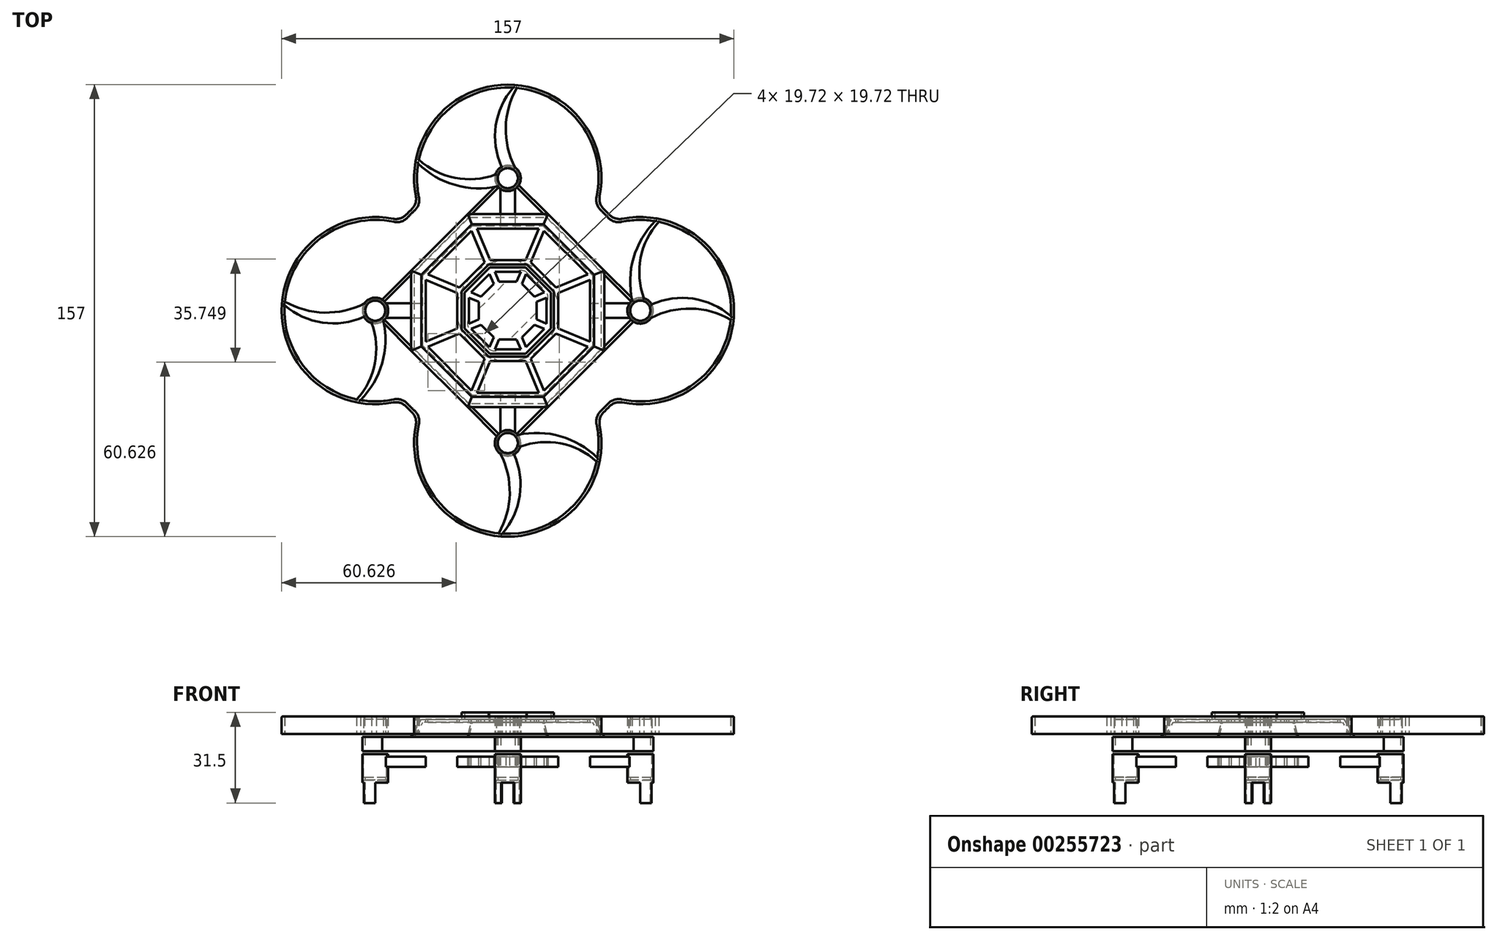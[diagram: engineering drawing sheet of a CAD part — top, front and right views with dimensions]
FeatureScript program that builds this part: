
annotation { "Feature Type Name" : "Feature", "Feature Type Description" : "" }
export const myFeature = defineFeature(function(context is Context, id is Id, definition is map)
    precondition{}
    {
        {
            var Q0;
            Q0=qCreatedBy(makeId("Top.planeOp"),FACE);
            var sketch = newSketch(context, id + "F0", { "sketchPlane" : qUnion([Q0])});
            skArc(sketch, "E0", {"start": v(4.7, -16.86) * mm, "mid": v(12.37, -12.37) * mm, "end": v(16.86, -4.7) * mm});
            skLineSegment(sketch, "E1.left", {"start": v(-2.5, 42.26) * mm, "end": v(-2.5, 19.75) * mm});
            skLineSegment(sketch, "E1.right", {"start": v(2.5, 42.26) * mm, "end": v(2.5, 19.75) * mm});
            skArc(sketch, "E2", {"start": v(42.26, -2.5) * mm, "mid": v(50.5, 0) * mm, "end": v(42.26, 2.5) * mm});
            skArc(sketch, "E3", {"start": v(-42.26, 2.5) * mm, "mid": v(-50.5, 0) * mm, "end": v(-42.26, -2.5) * mm});
            skArc(sketch, "E4", {"start": v(2.5, 42.26) * mm, "mid": v(0, 50.5) * mm, "end": v(-2.5, 42.26) * mm});
            skArc(sketch, "E5", {"start": v(-2.5, -42.26) * mm, "mid": v(0, -50.5) * mm, "end": v(2.5, -42.26) * mm});
            skArc(sketch, "E6.trimOffspring", {"start": v(-16.86, -4.7) * mm, "mid": v(-12.37, -12.37) * mm, "end": v(-4.7, -16.86) * mm});
            skArc(sketch, "E7.trimOffspring", {"start": v(16.86, 4.7) * mm, "mid": v(12.37, 12.37) * mm, "end": v(4.7, 16.86) * mm});
            skArc(sketch, "E8.trimOffspring", {"start": v(-4.7, 16.86) * mm, "mid": v(-12.37, 12.37) * mm, "end": v(-16.86, 4.7) * mm});
            skLineSegment(sketch, "E9", {"start": v(-42.26, 2.5) * mm, "end": v(-19.75, 2.5) * mm});
            skLineSegment(sketch, "E10", {"start": v(-42.26, -2.5) * mm, "end": v(-19.75, -2.5) * mm});
            skLineSegment(sketch, "E11", {"start": v(-42.26, 2.5) * mm, "end": v(-42.26, -2.5) * mm, "construction": true});
            skPoint(sketch, "E12", {"position": v(-42.26, 0) * mm});
            skLineSegment(sketch, "E13", {"start": v(-46, 0) * mm, "end": v(46, 0) * mm, "construction": true});
            skLineSegment(sketch, "E14", {"start": v(0, 46) * mm, "end": v(0, -46) * mm, "construction": true});
            skLineSegment(sketch, "E15", {"start": v(19.75, 2.5) * mm, "end": v(42.26, 2.5) * mm});
            skLineSegment(sketch, "E16", {"start": v(19.75, -2.5) * mm, "end": v(42.26, -2.5) * mm});
            skLineSegment(sketch, "E17", {"start": v(42.26, 2.5) * mm, "end": v(42.26, -2.5) * mm, "construction": true});
            skPoint(sketch, "E18", {"position": v(42.26, 0) * mm});
            skPoint(sketch, "E19.visualSharp", {"position": v(-17.32, 2.5) * mm});
            skArc(sketch, "E19.filletArc", {"start": v(-19.75, 2.5) * mm, "mid": v(-17.93, 3.11) * mm, "end": v(-16.86, 4.7) * mm});
            skPoint(sketch, "E20.visualSharp", {"position": v(17.32, 2.5) * mm});
            skArc(sketch, "E20.filletArc", {"start": v(16.86, 4.7) * mm, "mid": v(17.93, 3.11) * mm, "end": v(19.75, 2.5) * mm});
            skPoint(sketch, "E21.visualSharp", {"position": v(17.32, -2.5) * mm});
            skArc(sketch, "E21.filletArc", {"start": v(19.75, -2.5) * mm, "mid": v(17.93, -3.11) * mm, "end": v(16.86, -4.7) * mm});
            skPoint(sketch, "E22.visualSharp", {"position": v(-17.32, -2.5) * mm});
            skArc(sketch, "E22.filletArc", {"start": v(-16.86, -4.7) * mm, "mid": v(-17.93, -3.11) * mm, "end": v(-19.75, -2.5) * mm});
            skPoint(sketch, "E23.visualSharp", {"position": v(-2.5, 17.32) * mm});
            skArc(sketch, "E23.filletArc", {"start": v(-4.7, 16.86) * mm, "mid": v(-3.11, 17.93) * mm, "end": v(-2.5, 19.75) * mm});
            skPoint(sketch, "E24.visualSharp", {"position": v(2.5, 17.32) * mm});
            skArc(sketch, "E24.filletArc", {"start": v(2.5, 19.75) * mm, "mid": v(3.11, 17.93) * mm, "end": v(4.7, 16.86) * mm});
            skPoint(sketch, "E25.visualSharp", {"position": v(-2.5, -17.32) * mm});
            skArc(sketch, "E25.filletArc", {"start": v(-2.5, -19.75) * mm, "mid": v(-3.11, -17.93) * mm, "end": v(-4.7, -16.86) * mm});
            skPoint(sketch, "E26.visualSharp", {"position": v(2.5, -17.32) * mm});
            skArc(sketch, "E26.filletArc", {"start": v(4.7, -16.86) * mm, "mid": v(3.11, -17.93) * mm, "end": v(2.5, -19.75) * mm});
            skLineSegment(sketch, "E27", {"start": v(-2.5, -19.75) * mm, "end": v(-2.5, -42.26) * mm});
            skLineSegment(sketch, "E28", {"start": v(2.5, -19.75) * mm, "end": v(2.5, -42.26) * mm});
            skLineSegment(sketch, "E29", {"start": v(-2.5, -42.26) * mm, "end": v(2.5, -42.26) * mm, "construction": true});
            skPoint(sketch, "E30", {"position": v(0, -42.26) * mm});
            skLineSegment(sketch, "E31", {"start": v(-2.5, 42.26) * mm, "end": v(2.5, 42.26) * mm, "construction": true});
            skPoint(sketch, "E32", {"position": v(0, 42.26) * mm});
            skLineSegment(sketch, "E33", {"start": v(-13.08, -2.47) * mm, "end": v(2.47, 13.08) * mm});
            skLineSegment(sketch, "E34", {"start": v(6.72, 13.08) * mm, "end": v(13.08, 6.72) * mm});
            skLineSegment(sketch, "E35", {"start": v(13.08, 2.47) * mm, "end": v(-2.47, -13.08) * mm});
            skLineSegment(sketch, "E36", {"start": v(-6.72, -13.08) * mm, "end": v(-13.08, -6.72) * mm});
            skLineSegment(sketch, "E37", {"start": v(15.2, 4.6) * mm, "end": v(-15.2, -4.6) * mm, "construction": true});
            skLineSegment(sketch, "E38", {"start": v(4.6, 15.2) * mm, "end": v(-4.6, -15.2) * mm, "construction": true});
            skLineSegment(sketch, "E39", {"start": v(9.9, 9.9) * mm, "end": v(-9.9, -9.9) * mm, "construction": true});
            skPoint(sketch, "E40.visualSharp", {"position": v(4.6, 15.2) * mm});
            skArc(sketch, "E40.filletArc", {"start": v(6.72, 13.08) * mm, "mid": v(4.6, 13.96) * mm, "end": v(2.47, 13.08) * mm});
            skPoint(sketch, "E41.visualSharp", {"position": v(-15.2, -4.6) * mm});
            skArc(sketch, "E41.filletArc", {"start": v(-13.08, -2.47) * mm, "mid": v(-13.96, -4.6) * mm, "end": v(-13.08, -6.72) * mm});
            skPoint(sketch, "E42.visualSharp", {"position": v(-4.6, -15.2) * mm});
            skArc(sketch, "E42.filletArc", {"start": v(-6.72, -13.08) * mm, "mid": v(-4.6, -13.96) * mm, "end": v(-2.47, -13.08) * mm});
            skPoint(sketch, "E43.visualSharp", {"position": v(15.2, 4.6) * mm});
            skArc(sketch, "E43.filletArc", {"start": v(13.08, 2.47) * mm, "mid": v(13.96, 4.6) * mm, "end": v(13.08, 6.72) * mm});
            skSolve(sketch);
        }
        {
            var Q0;
            Q0=makeQuery(id+"F0.imprint","IMPRINT",FACE,{"disambiguationData":[TD([[makeQuery(id+"F0.imprint","IMPRINT",EDGE,{"derivedFrom":sQuery(id+"F0.wireOp",EDGE,"E0")}),1.0]])]});
            extrude(context, id + "F1", {"entities" : qUnion([Q0]), "depth" : 3.5 * mm});
        }
        {
            var Q0;
            Q0=makeQuery(id+"F1.opExtrude","CAP_FACE",FACE,{"disambiguationData":[OSD([sQuery(id+"F0.wireOp",EDGE,"E0"),sQuery(id+"F0.wireOp",EDGE,"E1.left"),sQuery(id+"F0.wireOp",EDGE,"E1.right"),sQuery(id+"F0.wireOp",EDGE,"E2"),sQuery(id+"F0.wireOp",EDGE,"E3"),sQuery(id+"F0.wireOp",EDGE,"E4"),sQuery(id+"F0.wireOp",EDGE,"E5"),sQuery(id+"F0.wireOp",EDGE,"E6.trimOffspring"),sQuery(id+"F0.wireOp",EDGE,"E7.trimOffspring"),sQuery(id+"F0.wireOp",EDGE,"E8.trimOffspring"),sQuery(id+"F0.wireOp",EDGE,"E9"),sQuery(id+"F0.wireOp",EDGE,"E10"),sQuery(id+"F0.wireOp",EDGE,"E15"),sQuery(id+"F0.wireOp",EDGE,"E16"),sQuery(id+"F0.wireOp",EDGE,"E19.filletArc"),sQuery(id+"F0.wireOp",EDGE,"E20.filletArc"),sQuery(id+"F0.wireOp",EDGE,"E21.filletArc"),sQuery(id+"F0.wireOp",EDGE,"E22.filletArc"),sQuery(id+"F0.wireOp",EDGE,"E23.filletArc"),sQuery(id+"F0.wireOp",EDGE,"E24.filletArc"),sQuery(id+"F0.wireOp",EDGE,"E25.filletArc"),sQuery(id+"F0.wireOp",EDGE,"E26.filletArc"),sQuery(id+"F0.wireOp",EDGE,"E27"),sQuery(id+"F0.wireOp",EDGE,"E28"),sQuery(id+"F0.wireOp",EDGE,"E33"),sQuery(id+"F0.wireOp",EDGE,"E34"),sQuery(id+"F0.wireOp",EDGE,"E35"),sQuery(id+"F0.wireOp",EDGE,"E36"),sQuery(id+"F0.wireOp",EDGE,"E40.filletArc"),sQuery(id+"F0.wireOp",EDGE,"E41.filletArc"),sQuery(id+"F0.wireOp",EDGE,"E42.filletArc"),sQuery(id+"F0.wireOp",EDGE,"E43.filletArc")])],"isStart":true});
            var sketch = newSketch(context, id + "F2", { "sketchPlane" : qUnion([Q0])});
            skCircle(sketch, "E44", {"center": v(-46, 0) * mm, "radius": 4.5 * mm});
            skCircle(sketch, "E45", {"center": v(0, 46) * mm, "radius": 4.5 * mm});
            skCircle(sketch, "E46", {"center": v(46, 0) * mm, "radius": 4.5 * mm});
            skCircle(sketch, "E47", {"center": v(0, -46) * mm, "radius": 4.5 * mm});
            skSolve(sketch);
        }
        {
            var Q0;
            Q0=qSketchRegion(id+"F2",true);
            extrude(context, id + "F3", {"entities" : qUnion([Q0]), "operationType" : NewBodyOperationType.ADD, "oppositeDirection" : true, "depth" : 4.45 * mm, "hasSecondDirection" : true, "secondDirectionOppositeDirection" : false, "secondDirectionDepth" : (10 - 4.45) * mm});
        }
        {
            var Q0;
            Q0=makeQuery(id+"F3.opExtrude","CAP_FACE",FACE,{"disambiguationData":[OSD([sQuery(id+"F2.wireOp",EDGE,"E45")])],"isStart":true});
            var sketch = newSketch(context, id + "F4", { "sketchPlane" : qUnion([Q0])});
            skArc(sketch, "E48", {"start": v(4.5, 46) * mm, "mid": v(3.9, 48.25) * mm, "end": v(2.25, 49.9) * mm});
            skArc(sketch, "E49", {"start": v(4, 46) * mm, "mid": v(3.46, 48) * mm, "end": v(2, 49.46) * mm});
            skLineSegment(sketch, "E50", {"start": v(2, 49.46) * mm, "end": v(2.25, 49.9) * mm});
            skLineSegment(sketch, "E51", {"start": v(-2, 49.46) * mm, "end": v(-2.25, 49.9) * mm});
            skLineSegment(sketch, "E52", {"start": v(-4, 46) * mm, "end": v(-4.5, 46) * mm});
            skLineSegment(sketch, "E53", {"start": v(4, 46) * mm, "end": v(4.5, 46) * mm});
            skLineSegment(sketch, "E54", {"start": v(0, 46) * mm, "end": v(0, 50.5) * mm, "construction": true});
            skArc(sketch, "E55.trimOffspring", {"start": v(-2, 49.46) * mm, "mid": v(-3.46, 48) * mm, "end": v(-4, 46) * mm});
            skArc(sketch, "E56.trimOffspring", {"start": v(-2.25, 49.9) * mm, "mid": v(-3.9, 48.25) * mm, "end": v(-4.5, 46) * mm});
            skLineSegment(sketch, "E57.1.0", {"start": v(-46, 0) * mm, "end": v(-50.5, 0) * mm, "construction": true});
            skArc(sketch, "E57.1.1", {"start": v(-46, 4.5) * mm, "mid": v(-48.25, 3.9) * mm, "end": v(-49.9, 2.25) * mm});
            skArc(sketch, "E57.1.2", {"start": v(-46, 4) * mm, "mid": v(-48, 3.46) * mm, "end": v(-49.46, 2) * mm});
            skArc(sketch, "E57.1.3", {"start": v(-49.9, -2.25) * mm, "mid": v(-48.25, -3.9) * mm, "end": v(-46, -4.5) * mm});
            skArc(sketch, "E57.1.4", {"start": v(-49.46, -2) * mm, "mid": v(-48, -3.46) * mm, "end": v(-46, -4) * mm});
            skLineSegment(sketch, "E57.1.5", {"start": v(-46, -4) * mm, "end": v(-46, -4.5) * mm});
            skLineSegment(sketch, "E57.1.6", {"start": v(-46, 4) * mm, "end": v(-46, 4.5) * mm});
            skLineSegment(sketch, "E57.1.7", {"start": v(-49.46, 2) * mm, "end": v(-49.9, 2.25) * mm});
            skLineSegment(sketch, "E57.1.8", {"start": v(-49.46, -2) * mm, "end": v(-49.9, -2.25) * mm});
            skLineSegment(sketch, "E57.2.0", {"start": v(0, -46) * mm, "end": v(0, -50.5) * mm, "construction": true});
            skArc(sketch, "E57.2.1", {"start": v(-4.5, -46) * mm, "mid": v(-3.9, -48.25) * mm, "end": v(-2.25, -49.9) * mm});
            skArc(sketch, "E57.2.2", {"start": v(-4, -46) * mm, "mid": v(-3.46, -48) * mm, "end": v(-2, -49.46) * mm});
            skArc(sketch, "E57.2.3", {"start": v(2.25, -49.9) * mm, "mid": v(3.9, -48.25) * mm, "end": v(4.5, -46) * mm});
            skArc(sketch, "E57.2.4", {"start": v(2, -49.46) * mm, "mid": v(3.46, -48) * mm, "end": v(4, -46) * mm});
            skLineSegment(sketch, "E57.2.5", {"start": v(4, -46) * mm, "end": v(4.5, -46) * mm});
            skLineSegment(sketch, "E57.2.6", {"start": v(-4, -46) * mm, "end": v(-4.5, -46) * mm});
            skLineSegment(sketch, "E57.2.7", {"start": v(-2, -49.46) * mm, "end": v(-2.25, -49.9) * mm});
            skLineSegment(sketch, "E57.2.8", {"start": v(2, -49.46) * mm, "end": v(2.25, -49.9) * mm});
            skLineSegment(sketch, "E57.3.0", {"start": v(46, 0) * mm, "end": v(50.5, 0) * mm, "construction": true});
            skArc(sketch, "E57.3.1", {"start": v(46, -4.5) * mm, "mid": v(48.25, -3.9) * mm, "end": v(49.9, -2.25) * mm});
            skArc(sketch, "E57.3.2", {"start": v(46, -4) * mm, "mid": v(48, -3.46) * mm, "end": v(49.46, -2) * mm});
            skArc(sketch, "E57.3.3", {"start": v(49.9, 2.25) * mm, "mid": v(48.25, 3.9) * mm, "end": v(46, 4.5) * mm});
            skArc(sketch, "E57.3.4", {"start": v(49.46, 2) * mm, "mid": v(48, 3.46) * mm, "end": v(46, 4) * mm});
            skLineSegment(sketch, "E57.3.5", {"start": v(46, 4) * mm, "end": v(46, 4.5) * mm});
            skLineSegment(sketch, "E57.3.6", {"start": v(46, -4) * mm, "end": v(46, -4.5) * mm});
            skLineSegment(sketch, "E57.3.7", {"start": v(49.46, -2) * mm, "end": v(49.9, -2.25) * mm});
            skLineSegment(sketch, "E57.3.8", {"start": v(49.46, 2) * mm, "end": v(49.9, 2.25) * mm});
            skPoint(sketch, "E57.center", {"position": v(0, 0) * mm});
            skSolve(sketch);
        }
        {
            var Q0;
            Q0=qSketchRegion(id+"F4",true);
            extrude(context, id + "F5", {"entities" : qUnion([Q0]), "operationType" : NewBodyOperationType.ADD, "depth" : 7 * mm});
        }
        {
            var Q0;
            Q0=makeQuery(id+"F3.opExtrude","CAP_FACE",FACE,{"disambiguationData":[OSD([sQuery(id+"F2.wireOp",EDGE,"E46")])],"isStart":true});
            var sketch = newSketch(context, id + "F6", { "sketchPlane" : qUnion([Q0])});
            skCircle(sketch, "E58", {"center": v(46, 0) * mm, "radius": 4 * mm});
            skCircle(sketch, "E59.1.0", {"center": v(0, 46) * mm, "radius": 4 * mm});
            skCircle(sketch, "E59.2.0", {"center": v(-46, 0) * mm, "radius": 4 * mm});
            skCircle(sketch, "E59.3.0", {"center": v(0, -46) * mm, "radius": 4 * mm});
            skPoint(sketch, "E59.center", {"position": v(0, 0) * mm});
            skSolve(sketch);
        }
        {
            var Q0;
            Q0=qSketchRegion(id+"F6",true);
            extrude(context, id + "F7", {"entities" : qUnion([Q0]), "operationType" : NewBodyOperationType.REMOVE, "endBound" : BoundingType.UP_TO_NEXT, "oppositeDirection" : true, "depth" : 25 * mm});
        }
        {
            var Q0;
            {var subQ0=sQuery(id+"F2.wireOp",EDGE,"E46");Q0=makeQuery(id+"F7.boolean.opBoolean","SPLIT",FACE,{"disambiguationData":[TD([makeQuery(id+"F5.opExtrude","SWEPT_FACE",FACE,{"disambiguationData":[OSD([sQuery(id+"F4.wireOp",EDGE,"E57.3.5")])]})])],"derivedFrom":makeQuery(id+"F3.opExtrude","CAP_FACE",FACE,{"disambiguationData":[OSD([subQ0])],"isStart":true})});}
            cPlane(context, id + "F8", {"entities" : qUnion([Q0]), "cplaneType" : CPlaneType.OFFSET, "offset" : 1 * mm, "oppositeDirection" : true, "width" : 150 * mm, "height" : 150 * mm});
        }
        {
            var Q0;
            Q0=qCreatedBy(id+"F8.planeOp",FACE);
            var sketch = newSketch(context, id + "F9", { "sketchPlane" : qUnion([Q0])});
            skCircle(sketch, "E60", {"center": v(46, 0) * mm, "radius": 4 * mm});
            skCircle(sketch, "E61", {"center": v(46, 0) * mm, "radius": 3.5 * mm});
            skCircle(sketch, "E62.1.0", {"center": v(0, 46) * mm, "radius": 3.5 * mm});
            skCircle(sketch, "E62.1.1", {"center": v(0, 46) * mm, "radius": 4 * mm});
            skCircle(sketch, "E62.2.0", {"center": v(-46, 0) * mm, "radius": 3.5 * mm});
            skCircle(sketch, "E62.2.1", {"center": v(-46, 0) * mm, "radius": 4 * mm});
            skCircle(sketch, "E62.3.0", {"center": v(0, -46) * mm, "radius": 3.5 * mm});
            skCircle(sketch, "E62.3.1", {"center": v(0, -46) * mm, "radius": 4 * mm});
            skPoint(sketch, "E62.center", {"position": v(0, 0) * mm});
            skSolve(sketch);
        }
        {
            var Q0;
            Q0=qSketchRegion(id+"F9",true);
            extrude(context, id + "F10", {"entities" : qUnion([Q0]), "operationType" : NewBodyOperationType.ADD, "oppositeDirection" : true, "depth" : 1 * mm});
        }
        {
            var Q0;
            Q0=makeQuery(id+"F3.opExtrude","CAP_FACE",FACE,{"disambiguationData":[OSD([sQuery(id+"F2.wireOp",EDGE,"E45")])],"isStart":false});
            cPlane(context, id + "F11", {"entities" : qUnion([Q0]), "cplaneType" : CPlaneType.OFFSET, "offset" : 7 * mm, "width" : 150 * mm, "height" : 150 * mm});
        }
        {
            var Q0;
            Q0=qCreatedBy(id+"F11.planeOp",FACE);
            var sketch = newSketch(context, id + "F12", { "sketchPlane" : qUnion([Q0])});
            skArc(sketch, "E63", {"start": v(3.5, -43.18) * mm, "mid": v(-3.32, -42.96) * mm, "end": v(-2.51, -49.73) * mm});
            skCircle(sketch, "E64", {"center": v(0, -46) * mm, "radius": 4 * mm});
            skArc(sketch, "E65", {"start": v(-30.1, -36.74) * mm, "mid": v(-26.23, -63.44) * mm, "end": v(-3.12, -77.35) * mm});
            skArc(sketch, "E66", {"start": v(30.1, -36.74) * mm, "mid": v(33.59, -33.59) * mm, "end": v(36.74, -30.1) * mm});
            skArc(sketch, "E67", {"start": v(49.95, 2.16) * mm, "mid": v(41.5, 0.2) * mm, "end": v(49.73, -2.51) * mm});
            skCircle(sketch, "E68", {"center": v(46, 0) * mm, "radius": 4 * mm});
            skCircle(sketch, "E69", {"center": v(0, 46) * mm, "radius": 4.5 * mm});
            skCircle(sketch, "E70", {"center": v(0, 46) * mm, "radius": 4 * mm});
            skCircle(sketch, "E71", {"center": v(-46, 0) * mm, "radius": 4.5 * mm});
            skCircle(sketch, "E72", {"center": v(-46, 0) * mm, "radius": 4 * mm});
            skArc(sketch, "E73", {"start": v(36.74, -30.1) * mm, "mid": v(63.44, -26.23) * mm, "end": v(77.35, -3.12) * mm});
            skArc(sketch, "E74", {"start": v(30.1, 36.74) * mm, "mid": v(0, 77.5) * mm, "end": v(-30.1, 36.74) * mm});
            skArc(sketch, "E75", {"start": v(-36.74, 30.1) * mm, "mid": v(-77.5, 0) * mm, "end": v(-36.74, -30.1) * mm});
            skArc(sketch, "E76.trimOffspring", {"start": v(36.74, 30.1) * mm, "mid": v(33.59, 33.59) * mm, "end": v(30.1, 36.74) * mm});
            skArc(sketch, "E77.trimOffspring", {"start": v(-30.1, 36.74) * mm, "mid": v(-33.59, 33.59) * mm, "end": v(-36.74, 30.1) * mm});
            skArc(sketch, "E78.trimOffspring", {"start": v(-36.74, -30.1) * mm, "mid": v(-33.59, -33.59) * mm, "end": v(-30.1, -36.74) * mm});
            skArc(sketch, "E79.0", {"start": v(-37.09, -31.25) * mm, "mid": v(-34.3, -34.3) * mm, "end": v(-31.25, -37.09) * mm});
            skArc(sketch, "E79.1", {"start": v(-37.09, 31.25) * mm, "mid": v(-78.5, 0) * mm, "end": v(-37.09, -31.25) * mm});
            skArc(sketch, "E79.2", {"start": v(-31.25, -37.09) * mm, "mid": v(0, -78.5) * mm, "end": v(31.25, -37.09) * mm});
            skArc(sketch, "E79.3", {"start": v(-31.25, 37.09) * mm, "mid": v(-34.3, 34.3) * mm, "end": v(-37.09, 31.25) * mm});
            skArc(sketch, "E79.4", {"start": v(31.25, -37.09) * mm, "mid": v(34.3, -34.3) * mm, "end": v(37.09, -31.25) * mm});
            skArc(sketch, "E79.5", {"start": v(37.09, -31.25) * mm, "mid": v(78.5, 0) * mm, "end": v(37.09, 31.25) * mm});
            skArc(sketch, "E79.6", {"start": v(37.09, 31.25) * mm, "mid": v(34.3, 34.3) * mm, "end": v(31.25, 37.09) * mm});
            skArc(sketch, "E79.7", {"start": v(31.25, 37.09) * mm, "mid": v(0, 78.5) * mm, "end": v(-31.25, 37.09) * mm});
            skArc(sketch, "E80", {"start": v(30.84, -52.42) * mm, "mid": v(18.3, -46.12) * mm, "end": v(4.32, -47.25) * mm});
            skArc(sketch, "E81", {"start": v(31.08, -51.12) * mm, "mid": v(18.3, -43.64) * mm, "end": v(3.5, -43.18) * mm});
            skArc(sketch, "E82", {"start": v(-1.88, -77.44) * mm, "mid": v(4.15, -64.29) * mm, "end": v(2.16, -49.95) * mm});
            skArc(sketch, "E83", {"start": v(-3.12, -77.35) * mm, "mid": v(0.69, -63.62) * mm, "end": v(-2.51, -49.73) * mm});
            skArc(sketch, "E84.1.0", {"start": v(52.42, 30.84) * mm, "mid": v(46.12, 18.3) * mm, "end": v(47.25, 4.32) * mm});
            skArc(sketch, "E84.1.1", {"start": v(51.12, 31.08) * mm, "mid": v(43.64, 18.3) * mm, "end": v(43.18, 3.5) * mm});
            skArc(sketch, "E84.1.2", {"start": v(77.44, -1.88) * mm, "mid": v(64.29, 4.15) * mm, "end": v(49.95, 2.16) * mm});
            skArc(sketch, "E84.1.3", {"start": v(77.35, -3.12) * mm, "mid": v(63.62, 0.69) * mm, "end": v(49.73, -2.51) * mm});
            skArc(sketch, "E84.2.0", {"start": v(-30.84, 52.42) * mm, "mid": v(-18.3, 46.12) * mm, "end": v(-4.32, 47.25) * mm});
            skArc(sketch, "E84.2.1", {"start": v(-31.08, 51.12) * mm, "mid": v(-18.3, 43.64) * mm, "end": v(-3.5, 43.18) * mm});
            skArc(sketch, "E84.2.2", {"start": v(1.88, 77.44) * mm, "mid": v(-4.15, 64.29) * mm, "end": v(-2.16, 49.95) * mm});
            skArc(sketch, "E84.2.3", {"start": v(3.12, 77.35) * mm, "mid": v(-0.69, 63.62) * mm, "end": v(2.51, 49.73) * mm});
            skArc(sketch, "E84.3.0", {"start": v(-52.42, -30.84) * mm, "mid": v(-46.12, -18.3) * mm, "end": v(-47.25, -4.32) * mm});
            skArc(sketch, "E84.3.1", {"start": v(-51.12, -31.08) * mm, "mid": v(-43.64, -18.3) * mm, "end": v(-43.18, -3.5) * mm});
            skArc(sketch, "E84.3.2", {"start": v(-77.44, 1.88) * mm, "mid": v(-64.29, -4.15) * mm, "end": v(-49.95, -2.16) * mm});
            skArc(sketch, "E84.3.3", {"start": v(-77.35, 3.12) * mm, "mid": v(-63.62, -0.69) * mm, "end": v(-49.73, 2.51) * mm});
            skArc(sketch, "E85.trimOffspring", {"start": v(31.08, -51.12) * mm, "mid": v(31.43, -43.88) * mm, "end": v(30.1, -36.74) * mm});
            skArc(sketch, "E86.trimOffspring", {"start": v(-1.88, -77.44) * mm, "mid": v(19.13, -71.02) * mm, "end": v(30.84, -52.42) * mm});
            skArc(sketch, "E87.trimOffspring", {"start": v(2.16, -49.95) * mm, "mid": v(3.51, -48.82) * mm, "end": v(4.32, -47.25) * mm});
            skArc(sketch, "E88.trimOffspring", {"start": v(77.44, -1.88) * mm, "mid": v(71.02, 19.13) * mm, "end": v(52.42, 30.84) * mm});
            skArc(sketch, "E89.trimOffspring", {"start": v(51.12, 31.08) * mm, "mid": v(43.88, 31.43) * mm, "end": v(36.74, 30.1) * mm});
            skSolve(sketch);
        }
        {
            var Q0;
            {var subQ0=sQuery(id+"F12.wireOp",EDGE,"E84.2.2");Q0=makeQuery(id+"F12.imprint","IMPRINT",FACE,{"disambiguationData":[TD([[makeQuery(id+"F12.imprint","IMPRINT",EDGE,{"derivedFrom":subQ0}),1.0]])]});}
            var Q1;
            Q1=makeQuery(id+"F12.imprint","IMPRINT",FACE,{"disambiguationData":[TD([[makeQuery(id+"F12.imprint","IMPRINT",EDGE,{"derivedFrom":sQuery(id+"F12.wireOp",EDGE,"E70")}),-1.0]])]});
            var Q2;
            {var subQ0=sQuery(id+"F12.wireOp",EDGE,"E84.2.0");Q2=makeQuery(id+"F12.imprint","IMPRINT",FACE,{"disambiguationData":[TD([[makeQuery(id+"F12.imprint","IMPRINT",EDGE,{"derivedFrom":subQ0}),-1.0]])]});}
            var Q3;
            Q3=makeQuery(id+"F12.imprint","IMPRINT",FACE,{"disambiguationData":[TD([[makeQuery(id+"F12.imprint","IMPRINT",EDGE,{"derivedFrom":sQuery(id+"F12.wireOp",EDGE,"E63")}),1.0]])]});
            var Q4;
            {var subQ0=sQuery(id+"F12.wireOp",EDGE,"E84.3.0");Q4=makeQuery(id+"F12.imprint","IMPRINT",FACE,{"disambiguationData":[TD([[makeQuery(id+"F12.imprint","IMPRINT",EDGE,{"derivedFrom":subQ0}),-1.0]])]});}
            var Q5;
            {var subQ0=sQuery(id+"F12.wireOp",EDGE,"E84.3.2");Q5=makeQuery(id+"F12.imprint","IMPRINT",FACE,{"disambiguationData":[TD([[makeQuery(id+"F12.imprint","IMPRINT",EDGE,{"derivedFrom":subQ0}),1.0]])]});}
            var Q6;
            Q6=makeQuery(id+"F12.imprint","IMPRINT",FACE,{"disambiguationData":[TD([[makeQuery(id+"F12.imprint","IMPRINT",EDGE,{"derivedFrom":sQuery(id+"F12.wireOp",EDGE,"E72")}),-1.0]])]});
            extrude(context, id + "F13", {"entities" : qUnion([Q0, Q1, Q2, Q3, Q4, Q5, Q6]), "depth" : 6 * mm});
        }
        {
            var Q0;
            Q0=makeQuery(id+"F13.opExtrude","SWEPT_EDGE",EDGE,{"disambiguationData":[OSD([sQuery(id+"F12.wireOp",EDGE,"E66"),sQuery(id+"F12.wireOp",EDGE,"E73")])]});
            var Q1;
            Q1=makeQuery(id+"F13.opExtrude","SWEPT_EDGE",EDGE,{"disambiguationData":[OSD([sQuery(id+"F12.wireOp",EDGE,"E66"),sQuery(id+"F12.wireOp",EDGE,"E85.trimOffspring")])]});
            var Q2;
            Q2=makeQuery(id+"F13.opExtrude","SWEPT_EDGE",EDGE,{"disambiguationData":[OSD([sQuery(id+"F12.wireOp",EDGE,"E79.4"),sQuery(id+"F12.wireOp",EDGE,"E79.5")])]});
            var Q3;
            Q3=makeQuery(id+"F13.opExtrude","SWEPT_EDGE",EDGE,{"disambiguationData":[OSD([sQuery(id+"F12.wireOp",EDGE,"E79.2"),sQuery(id+"F12.wireOp",EDGE,"E79.4")])]});
            var Q4;
            Q4=makeQuery(id+"F13.opExtrude","SWEPT_EDGE",EDGE,{"disambiguationData":[OSD([sQuery(id+"F12.wireOp",EDGE,"E75"),sQuery(id+"F12.wireOp",EDGE,"E78.trimOffspring")])]});
            var Q5;
            Q5=makeQuery(id+"F13.opExtrude","SWEPT_EDGE",EDGE,{"disambiguationData":[OSD([sQuery(id+"F12.wireOp",EDGE,"E65"),sQuery(id+"F12.wireOp",EDGE,"E78.trimOffspring")])]});
            var Q6;
            Q6=makeQuery(id+"F13.opExtrude","SWEPT_EDGE",EDGE,{"disambiguationData":[OSD([sQuery(id+"F12.wireOp",EDGE,"E79.0"),sQuery(id+"F12.wireOp",EDGE,"E79.2")])]});
            var Q7;
            Q7=makeQuery(id+"F13.opExtrude","SWEPT_EDGE",EDGE,{"disambiguationData":[OSD([sQuery(id+"F12.wireOp",EDGE,"E79.0"),sQuery(id+"F12.wireOp",EDGE,"E79.1")])]});
            var Q8;
            Q8=makeQuery(id+"F13.opExtrude","SWEPT_EDGE",EDGE,{"disambiguationData":[OSD([sQuery(id+"F12.wireOp",EDGE,"E79.1"),sQuery(id+"F12.wireOp",EDGE,"E79.3")])]});
            var Q9;
            Q9=makeQuery(id+"F13.opExtrude","SWEPT_EDGE",EDGE,{"disambiguationData":[OSD([sQuery(id+"F12.wireOp",EDGE,"E79.3"),sQuery(id+"F12.wireOp",EDGE,"E79.7")])]});
            var Q10;
            Q10=makeQuery(id+"F13.opExtrude","SWEPT_EDGE",EDGE,{"disambiguationData":[OSD([sQuery(id+"F12.wireOp",EDGE,"E75"),sQuery(id+"F12.wireOp",EDGE,"E77.trimOffspring")])]});
            var Q11;
            Q11=makeQuery(id+"F13.opExtrude","SWEPT_EDGE",EDGE,{"disambiguationData":[OSD([sQuery(id+"F12.wireOp",EDGE,"E74"),sQuery(id+"F12.wireOp",EDGE,"E77.trimOffspring")])]});
            var Q12;
            Q12=makeQuery(id+"F13.opExtrude","SWEPT_EDGE",EDGE,{"disambiguationData":[OSD([sQuery(id+"F12.wireOp",EDGE,"E74"),sQuery(id+"F12.wireOp",EDGE,"E76.trimOffspring")])]});
            var Q13;
            Q13=makeQuery(id+"F13.opExtrude","SWEPT_EDGE",EDGE,{"disambiguationData":[OSD([sQuery(id+"F12.wireOp",EDGE,"E76.trimOffspring"),sQuery(id+"F12.wireOp",EDGE,"E89.trimOffspring")])]});
            var Q14;
            Q14=makeQuery(id+"F13.opExtrude","SWEPT_EDGE",EDGE,{"disambiguationData":[OSD([sQuery(id+"F12.wireOp",EDGE,"E79.6"),sQuery(id+"F12.wireOp",EDGE,"E79.7")])]});
            var Q15;
            Q15=makeQuery(id+"F13.opExtrude","SWEPT_EDGE",EDGE,{"disambiguationData":[OSD([sQuery(id+"F12.wireOp",EDGE,"E79.5"),sQuery(id+"F12.wireOp",EDGE,"E79.6")])]});
            fillet(context, id + "F14", {"entities" : qUnion([Q0, Q1, Q2, Q3, Q4, Q5, Q6, Q7, Q8, Q9, Q10, Q11, Q12, Q13, Q14, Q15]), "radius" : 5 * mm, "tangentPropagation" : true, "allowEdgeOverflow" : false});
        }
        {
            var Q0;
            Q0=makeQuery(id+"F13.opExtrude","CAP_FACE",FACE,{"disambiguationData":[OSD([sQuery(id+"F12.wireOp",EDGE,"E63"),sQuery(id+"F12.wireOp",EDGE,"E64"),sQuery(id+"F12.wireOp",EDGE,"E65"),sQuery(id+"F12.wireOp",EDGE,"E66"),sQuery(id+"F12.wireOp",EDGE,"E67"),sQuery(id+"F12.wireOp",EDGE,"E68"),sQuery(id+"F12.wireOp",EDGE,"E69"),sQuery(id+"F12.wireOp",EDGE,"E70"),sQuery(id+"F12.wireOp",EDGE,"E71"),sQuery(id+"F12.wireOp",EDGE,"E72"),sQuery(id+"F12.wireOp",EDGE,"E73"),sQuery(id+"F12.wireOp",EDGE,"E74"),sQuery(id+"F12.wireOp",EDGE,"E75"),sQuery(id+"F12.wireOp",EDGE,"E76.trimOffspring"),sQuery(id+"F12.wireOp",EDGE,"E77.trimOffspring"),sQuery(id+"F12.wireOp",EDGE,"E78.trimOffspring"),sQuery(id+"F12.wireOp",EDGE,"E79.0"),sQuery(id+"F12.wireOp",EDGE,"E79.1"),sQuery(id+"F12.wireOp",EDGE,"E79.2"),sQuery(id+"F12.wireOp",EDGE,"E79.3"),sQuery(id+"F12.wireOp",EDGE,"E79.4"),sQuery(id+"F12.wireOp",EDGE,"E79.5"),sQuery(id+"F12.wireOp",EDGE,"E79.6"),sQuery(id+"F12.wireOp",EDGE,"E79.7"),sQuery(id+"F12.wireOp",EDGE,"E80"),sQuery(id+"F12.wireOp",EDGE,"E81"),sQuery(id+"F12.wireOp",EDGE,"E82"),sQuery(id+"F12.wireOp",EDGE,"E83"),sQuery(id+"F12.wireOp",EDGE,"E84.1.0"),sQuery(id+"F12.wireOp",EDGE,"E84.1.1"),sQuery(id+"F12.wireOp",EDGE,"E84.1.2"),sQuery(id+"F12.wireOp",EDGE,"E84.1.3"),sQuery(id+"F12.wireOp",EDGE,"E84.2.0"),sQuery(id+"F12.wireOp",EDGE,"E84.2.1"),sQuery(id+"F12.wireOp",EDGE,"E84.2.2"),sQuery(id+"F12.wireOp",EDGE,"E84.2.3"),sQuery(id+"F12.wireOp",EDGE,"E84.3.0"),sQuery(id+"F12.wireOp",EDGE,"E84.3.1"),sQuery(id+"F12.wireOp",EDGE,"E84.3.2"),sQuery(id+"F12.wireOp",EDGE,"E84.3.3"),sQuery(id+"F12.wireOp",EDGE,"E85.trimOffspring"),sQuery(id+"F12.wireOp",EDGE,"E86.trimOffspring"),sQuery(id+"F12.wireOp",EDGE,"E87.trimOffspring"),sQuery(id+"F12.wireOp",EDGE,"E88.trimOffspring"),sQuery(id+"F12.wireOp",EDGE,"E89.trimOffspring")])],"isStart":false});
            var sketch = newSketch(context, id + "F15", { "sketchPlane" : qUnion([Q0])});
            skCircle(sketch, "E90", {"center": v(0, -46) * mm, "radius": 4.5 * mm});
            skCircle(sketch, "E91", {"center": v(0, -46) * mm, "radius": 3.5 * mm});
            skCircle(sketch, "E92.1.0", {"center": v(46, 0) * mm, "radius": 4.5 * mm});
            skCircle(sketch, "E92.1.1", {"center": v(46, 0) * mm, "radius": 3.5 * mm});
            skCircle(sketch, "E92.2.0", {"center": v(0, 46) * mm, "radius": 4.5 * mm});
            skCircle(sketch, "E92.2.1", {"center": v(0, 46) * mm, "radius": 3.5 * mm});
            skCircle(sketch, "E92.3.0", {"center": v(-46, 0) * mm, "radius": 4.5 * mm});
            skCircle(sketch, "E92.3.1", {"center": v(-46, 0) * mm, "radius": 3.5 * mm});
            skPoint(sketch, "E92.center", {"position": v(0, 0) * mm});
            skSolve(sketch);
        }
        {
            var Q0;
            Q0=qSketchRegion(id+"F15",true);
            extrude(context, id + "F16", {"entities" : qUnion([Q0]), "operationType" : NewBodyOperationType.ADD, "oppositeDirection" : true, "depth" : 1 * mm});
        }
        {
            var Q0;
            Q0=makeQuery(id+"F16.boolean.opBoolean","MERGE",FACE,{"derivedFrom":[makeQuery(id+"F13.opExtrude","CAP_FACE",FACE,{"disambiguationData":[OSD([sQuery(id+"F12.wireOp",EDGE,"E63"),sQuery(id+"F12.wireOp",EDGE,"E64"),sQuery(id+"F12.wireOp",EDGE,"E65"),sQuery(id+"F12.wireOp",EDGE,"E66"),sQuery(id+"F12.wireOp",EDGE,"E67"),sQuery(id+"F12.wireOp",EDGE,"E68"),sQuery(id+"F12.wireOp",EDGE,"E69"),sQuery(id+"F12.wireOp",EDGE,"E70"),sQuery(id+"F12.wireOp",EDGE,"E71"),sQuery(id+"F12.wireOp",EDGE,"E72"),sQuery(id+"F12.wireOp",EDGE,"E73"),sQuery(id+"F12.wireOp",EDGE,"E74"),sQuery(id+"F12.wireOp",EDGE,"E75"),sQuery(id+"F12.wireOp",EDGE,"E76.trimOffspring"),sQuery(id+"F12.wireOp",EDGE,"E77.trimOffspring"),sQuery(id+"F12.wireOp",EDGE,"E78.trimOffspring"),sQuery(id+"F12.wireOp",EDGE,"E79.0"),sQuery(id+"F12.wireOp",EDGE,"E79.1"),sQuery(id+"F12.wireOp",EDGE,"E79.2"),sQuery(id+"F12.wireOp",EDGE,"E79.3"),sQuery(id+"F12.wireOp",EDGE,"E79.4"),sQuery(id+"F12.wireOp",EDGE,"E79.5"),sQuery(id+"F12.wireOp",EDGE,"E79.6"),sQuery(id+"F12.wireOp",EDGE,"E79.7"),sQuery(id+"F12.wireOp",EDGE,"E80"),sQuery(id+"F12.wireOp",EDGE,"E81"),sQuery(id+"F12.wireOp",EDGE,"E82"),sQuery(id+"F12.wireOp",EDGE,"E83"),sQuery(id+"F12.wireOp",EDGE,"E84.1.0"),sQuery(id+"F12.wireOp",EDGE,"E84.1.1"),sQuery(id+"F12.wireOp",EDGE,"E84.1.2"),sQuery(id+"F12.wireOp",EDGE,"E84.1.3"),sQuery(id+"F12.wireOp",EDGE,"E84.2.0"),sQuery(id+"F12.wireOp",EDGE,"E84.2.1"),sQuery(id+"F12.wireOp",EDGE,"E84.2.2"),sQuery(id+"F12.wireOp",EDGE,"E84.2.3"),sQuery(id+"F12.wireOp",EDGE,"E84.3.0"),sQuery(id+"F12.wireOp",EDGE,"E84.3.1"),sQuery(id+"F12.wireOp",EDGE,"E84.3.2"),sQuery(id+"F12.wireOp",EDGE,"E84.3.3"),sQuery(id+"F12.wireOp",EDGE,"E85.trimOffspring"),sQuery(id+"F12.wireOp",EDGE,"E86.trimOffspring"),sQuery(id+"F12.wireOp",EDGE,"E87.trimOffspring"),sQuery(id+"F12.wireOp",EDGE,"E88.trimOffspring"),sQuery(id+"F12.wireOp",EDGE,"E89.trimOffspring")])],"isStart":false}),makeQuery(id+"F16.opExtrude","CAP_FACE",FACE,{"disambiguationData":[OSD([sQuery(id+"F15.wireOp",EDGE,"E90"),sQuery(id+"F15.wireOp",EDGE,"E91")])],"isStart":true}),makeQuery(id+"F16.opExtrude","CAP_FACE",FACE,{"disambiguationData":[OSD([sQuery(id+"F15.wireOp",EDGE,"E92.1.0"),sQuery(id+"F15.wireOp",EDGE,"E92.1.1")])],"isStart":true}),makeQuery(id+"F16.opExtrude","CAP_FACE",FACE,{"disambiguationData":[OSD([sQuery(id+"F15.wireOp",EDGE,"E92.2.0"),sQuery(id+"F15.wireOp",EDGE,"E92.2.1")])],"isStart":true}),makeQuery(id+"F16.opExtrude","CAP_FACE",FACE,{"disambiguationData":[OSD([sQuery(id+"F15.wireOp",EDGE,"E92.3.0"),sQuery(id+"F15.wireOp",EDGE,"E92.3.1")])],"isStart":true})]});
            fillet(context, id + "F17", {"entities" : qUnion([Q0]), "radius" : 0.3 * mm, "tangentPropagation" : true, "allowEdgeOverflow" : false});
        }
        {
            var Q0;
            Q0=makeQuery(id+"F3.opExtrude","CAP_FACE",FACE,{"disambiguationData":[OSD([sQuery(id+"F2.wireOp",EDGE,"E45")])],"isStart":false});
            cPlane(context, id + "F18", {"entities" : qUnion([Q0]), "cplaneType" : CPlaneType.OFFSET, "offset" : 1 * mm, "width" : 150 * mm, "height" : 150 * mm});
        }
        {
            var Q0;
            Q0=qCreatedBy(id+"F18.planeOp",FACE);
            var sketch = newSketch(context, id + "F19", { "sketchPlane" : qUnion([Q0])});
            skCircle(sketch, "E93", {"center": v(0, -46) * mm, "radius": 4.5 * mm});
            skCircle(sketch, "E94", {"center": v(0, -46) * mm, "radius": 3.5 * mm});
            skCircle(sketch, "E95.1.0", {"center": v(46, 0) * mm, "radius": 4.5 * mm});
            skCircle(sketch, "E95.1.1", {"center": v(46, 0) * mm, "radius": 3.5 * mm});
            skCircle(sketch, "E95.2.0", {"center": v(0, 46) * mm, "radius": 4.5 * mm});
            skCircle(sketch, "E95.2.1", {"center": v(0, 46) * mm, "radius": 3.5 * mm});
            skCircle(sketch, "E95.3.0", {"center": v(-46, 0) * mm, "radius": 4.5 * mm});
            skCircle(sketch, "E95.3.1", {"center": v(-46, 0) * mm, "radius": 3.5 * mm});
            skPoint(sketch, "E95.center", {"position": v(0, 0) * mm});
            skLineSegment(sketch, "E96", {"start": v(0, -46) * mm, "end": v(-46, 0) * mm});
            skLineSegment(sketch, "E97", {"start": v(-46, 0) * mm, "end": v(0, 46) * mm});
            skLineSegment(sketch, "E98", {"start": v(0, 46) * mm, "end": v(46, 0) * mm});
            skLineSegment(sketch, "E99", {"start": v(46, 0) * mm, "end": v(0, -46) * mm});
            skLineSegment(sketch, "E100.0", {"start": v(0, -44.59) * mm, "end": v(-44.59, 0) * mm, "construction": true});
            skLineSegment(sketch, "E100.1", {"start": v(44.59, 0) * mm, "end": v(0, -44.59) * mm, "construction": true});
            skLineSegment(sketch, "E100.2", {"start": v(0, 44.59) * mm, "end": v(44.59, 0) * mm, "construction": true});
            skLineSegment(sketch, "E100.3", {"start": v(-44.59, 0) * mm, "end": v(0, 44.59) * mm, "construction": true});
            skLineSegment(sketch, "E101.0", {"start": v(0, -47.41) * mm, "end": v(-47.41, 0) * mm});
            skLineSegment(sketch, "E101.1", {"start": v(47.41, 0) * mm, "end": v(0, -47.41) * mm});
            skLineSegment(sketch, "E101.2", {"start": v(0, 47.41) * mm, "end": v(47.41, 0) * mm});
            skLineSegment(sketch, "E101.3", {"start": v(-47.41, 0) * mm, "end": v(0, 47.41) * mm});
            skSolve(sketch);
        }
        {
            var Q0;
            Q0=qSketchRegion(id+"F19",true);
            extrude(context, id + "F20", {"entities" : qUnion([Q0]), "depth" : 5 * mm});
        }
        {
            var Q0;
            Q0=makeQuery(id+"F20.opExtrude","CAP_FACE",FACE,{"disambiguationData":[OSD([sQuery(id+"F19.wireOp",EDGE,"E93"),sQuery(id+"F19.wireOp",EDGE,"E94"),sQuery(id+"F19.wireOp",EDGE,"E95.1.0"),sQuery(id+"F19.wireOp",EDGE,"E95.1.1"),sQuery(id+"F19.wireOp",EDGE,"E95.2.0"),sQuery(id+"F19.wireOp",EDGE,"E95.2.1"),sQuery(id+"F19.wireOp",EDGE,"E95.3.0"),sQuery(id+"F19.wireOp",EDGE,"E95.3.1"),sQuery(id+"F19.wireOp",EDGE,"E96"),sQuery(id+"F19.wireOp",EDGE,"E97"),sQuery(id+"F19.wireOp",EDGE,"E98"),sQuery(id+"F19.wireOp",EDGE,"E99"),sQuery(id+"F19.wireOp",EDGE,"E101.0"),sQuery(id+"F19.wireOp",EDGE,"E101.1"),sQuery(id+"F19.wireOp",EDGE,"E101.2"),sQuery(id+"F19.wireOp",EDGE,"E101.3")])],"isStart":false});
            cPlane(context, id + "F21", {"entities" : qUnion([Q0]), "cplaneType" : CPlaneType.OFFSET, "offset" : 0 * mm, "width" : 150 * mm, "height" : 150 * mm});
        }
        {
            var Q0;
            Q0=qCreatedBy(id+"F21.planeOp",FACE);
            var sketch = newSketch(context, id + "F22", { "sketchPlane" : qUnion([Q0])});
            skCircle(sketch, "E102.cCircle", {"center": v(0, 0) * mm, "radius": 33.53 * mm, "construction": true});
            skLineSegment(sketch, "E102.0", {"start": v(13.89, -33.53) * mm, "end": v(-13.89, -33.53) * mm});
            skLineSegment(sketch, "E102.1", {"start": v(-13.89, -33.53) * mm, "end": v(-33.53, -13.89) * mm});
            skLineSegment(sketch, "E102.2", {"start": v(-33.53, -13.89) * mm, "end": v(-33.53, 13.89) * mm});
            skLineSegment(sketch, "E102.3", {"start": v(-33.53, 13.89) * mm, "end": v(-13.89, 33.53) * mm});
            skLineSegment(sketch, "E102.4", {"start": v(-13.89, 33.53) * mm, "end": v(13.89, 33.53) * mm});
            skLineSegment(sketch, "E102.5", {"start": v(13.89, 33.53) * mm, "end": v(33.53, 13.89) * mm});
            skLineSegment(sketch, "E102.6", {"start": v(33.53, 13.89) * mm, "end": v(33.53, -13.89) * mm});
            skLineSegment(sketch, "E102.7", {"start": v(33.53, -13.89) * mm, "end": v(13.89, -33.53) * mm});
            skPoint(sketch, "E102.0.midPoint", {"position": v(0, -33.53) * mm});
            skSolve(sketch);
        }
        {
            var Q0;
            Q0=qCreatedBy(id+"F21.planeOp",FACE);
            cPlane(context, id + "F23", {"entities" : qUnion([Q0]), "cplaneType" : CPlaneType.OFFSET, "offset" : 6 * mm, "width" : 150 * mm, "height" : 150 * mm});
        }
        {
            var Q0;
            Q0=qCreatedBy(id+"F23.planeOp",FACE);
            var sketch = newSketch(context, id + "F24", { "sketchPlane" : qUnion([Q0])});
            skCircle(sketch, "E103.cCircle", {"center": v(0, 0) * mm, "radius": 30 * mm, "construction": true});
            skLineSegment(sketch, "E103.0", {"start": v(12.43, -30) * mm, "end": v(-12.43, -30) * mm});
            skLineSegment(sketch, "E103.1", {"start": v(-12.43, -30) * mm, "end": v(-30, -12.43) * mm});
            skLineSegment(sketch, "E103.2", {"start": v(-30, -12.43) * mm, "end": v(-30, 12.43) * mm});
            skLineSegment(sketch, "E103.3", {"start": v(-30, 12.43) * mm, "end": v(-12.43, 30) * mm});
            skLineSegment(sketch, "E103.4", {"start": v(-12.43, 30) * mm, "end": v(12.43, 30) * mm});
            skLineSegment(sketch, "E103.5", {"start": v(12.43, 30) * mm, "end": v(30, 12.43) * mm});
            skLineSegment(sketch, "E103.6", {"start": v(30, 12.43) * mm, "end": v(30, -12.43) * mm});
            skLineSegment(sketch, "E103.7", {"start": v(30, -12.43) * mm, "end": v(12.43, -30) * mm});
            skPoint(sketch, "E103.0.midPoint", {"position": v(0, -30) * mm});
            skSolve(sketch);
        }
        {
            var Q1;
            Q1=makeQuery(id+"F22.imprint","IMPRINT",FACE,{"disambiguationData":[TD([[makeQuery(id+"F22.imprint","IMPRINT",EDGE,{"derivedFrom":sQuery(id+"F22.wireOp",EDGE,"E102.0")}),-1.0]])]});
            var Q2;
            Q2=makeQuery(id+"F24.imprint","IMPRINT",FACE,{"disambiguationData":[TD([[makeQuery(id+"F24.imprint","IMPRINT",EDGE,{"derivedFrom":sQuery(id+"F24.wireOp",EDGE,"E103.0")}),-1.0]])]});
            loft(context, id + "F25", {"operationType" : NewBodyOperationType.ADD, "sheetProfilesArray" : [{ "sheetProfileEntities" : qUnion([Q1]) }, { "sheetProfileEntities" : qUnion([Q2]) }]});
        }
        {
            var Q0;
            Q0=makeQuery(id+"F25.opLoft","CAP_FACE",FACE,{"disambiguationData":[OSD([makeQuery(id+"F22.imprint","IMPRINT",FACE,{"disambiguationData":[TD([[makeQuery(id+"F22.imprint","IMPRINT",EDGE,{"derivedFrom":sQuery(id+"F22.wireOp",EDGE,"E102.0")}),-1.0]])]})])],"isStart":true});
            shell(context, id + "F26", {"entities" : qUnion([Q0]), "thickness" : 1 * mm});
        }
        {
            var Q0;
            Q0=qCreatedBy(id+"F23.planeOp",FACE);
            var sketch = newSketch(context, id + "F27", { "sketchPlane" : qUnion([Q0])});
            skCircle(sketch, "E104.cCircle", {"center": v(0, 0) * mm, "radius": 16 * mm, "construction": true});
            skLineSegment(sketch, "E104.0", {"start": v(-16, 6.63) * mm, "end": v(-6.63, 16) * mm});
            skLineSegment(sketch, "E104.1", {"start": v(-6.63, 16) * mm, "end": v(6.63, 16) * mm});
            skLineSegment(sketch, "E104.2", {"start": v(6.63, 16) * mm, "end": v(16, 6.63) * mm});
            skLineSegment(sketch, "E104.3", {"start": v(16, 6.63) * mm, "end": v(16, -6.63) * mm});
            skLineSegment(sketch, "E104.4", {"start": v(16, -6.63) * mm, "end": v(6.63, -16) * mm});
            skLineSegment(sketch, "E104.5", {"start": v(6.63, -16) * mm, "end": v(-6.63, -16) * mm});
            skLineSegment(sketch, "E104.6", {"start": v(-6.63, -16) * mm, "end": v(-16, -6.63) * mm});
            skLineSegment(sketch, "E104.7", {"start": v(-16, -6.63) * mm, "end": v(-16, 6.63) * mm});
            skPoint(sketch, "E104.0.midPoint", {"position": v(-11.31, 11.31) * mm});
            skPoint(sketch, "E105", {"position": v(0, -46) * mm});
            skCircle(sketch, "E106.cCircle", {"center": v(0, 0) * mm, "radius": 15 * mm, "construction": true});
            skLineSegment(sketch, "E106.0", {"start": v(-15, -6.21) * mm, "end": v(-15, 6.21) * mm});
            skLineSegment(sketch, "E106.1", {"start": v(-15, 6.21) * mm, "end": v(-6.21, 15) * mm});
            skLineSegment(sketch, "E106.2", {"start": v(-6.21, 15) * mm, "end": v(6.21, 15) * mm});
            skLineSegment(sketch, "E106.3", {"start": v(6.21, 15) * mm, "end": v(15, 6.21) * mm});
            skLineSegment(sketch, "E106.4", {"start": v(15, 6.21) * mm, "end": v(15, -6.21) * mm});
            skLineSegment(sketch, "E106.5", {"start": v(15, -6.21) * mm, "end": v(6.21, -15) * mm});
            skLineSegment(sketch, "E106.6", {"start": v(6.21, -15) * mm, "end": v(-6.21, -15) * mm});
            skLineSegment(sketch, "E106.7", {"start": v(-6.21, -15) * mm, "end": v(-15, -6.21) * mm});
            skPoint(sketch, "E106.0.midPoint", {"position": v(-15, 0) * mm});
            skSolve(sketch);
        }
        {
            var Q0;
            Q0=qSketchRegion(id+"F27",true);
            extrude(context, id + "F28", {"entities" : qUnion([Q0]), "operationType" : NewBodyOperationType.ADD, "depth" : 2.5 * mm});
        }
        {
            var Q0;
            Q0=qCreatedBy(id+"F23.planeOp",FACE);
            var sketch = newSketch(context, id + "F29", { "sketchPlane" : qUnion([Q0])});
            skLineSegment(sketch, "E107", {"start": v(0, 0) * mm, "end": v(30, 12.43) * mm, "construction": true});
            skLineSegment(sketch, "E108", {"start": v(0, 0) * mm, "end": v(30, -12.43) * mm, "construction": true});
            skLineSegment(sketch, "E109", {"start": v(28.5, 10.72) * mm, "end": v(28.5, -10.72) * mm});
            skLineSegment(sketch, "E110", {"start": v(28.5, -10.72) * mm, "end": v(17.5, -6.17) * mm});
            skLineSegment(sketch, "E111", {"start": v(17.5, -6.17) * mm, "end": v(17.5, 6.17) * mm});
            skLineSegment(sketch, "E112", {"start": v(17.5, 6.17) * mm, "end": v(28.5, 10.72) * mm});
            skLineSegment(sketch, "E113", {"start": v(13.5, 4.5) * mm, "end": v(13.5, -4.5) * mm});
            skLineSegment(sketch, "E114", {"start": v(13.5, -4.5) * mm, "end": v(10, -3.06) * mm});
            skLineSegment(sketch, "E115", {"start": v(10, -3.06) * mm, "end": v(10, 3.06) * mm});
            skLineSegment(sketch, "E116", {"start": v(10, 3.06) * mm, "end": v(13.5, 4.5) * mm});
            skLineSegment(sketch, "E117.1.0", {"start": v(12.57, 27.73) * mm, "end": v(27.73, 12.57) * mm});
            skLineSegment(sketch, "E117.1.1", {"start": v(8.01, 16.73) * mm, "end": v(12.57, 27.73) * mm});
            skLineSegment(sketch, "E117.1.2", {"start": v(16.73, 8.01) * mm, "end": v(8.01, 16.73) * mm});
            skLineSegment(sketch, "E117.1.3", {"start": v(27.73, 12.57) * mm, "end": v(16.73, 8.01) * mm});
            skLineSegment(sketch, "E117.1.4", {"start": v(6.36, 12.73) * mm, "end": v(12.73, 6.36) * mm});
            skLineSegment(sketch, "E117.1.5", {"start": v(4.9, 9.23) * mm, "end": v(6.36, 12.73) * mm});
            skLineSegment(sketch, "E117.1.6", {"start": v(9.23, 4.9) * mm, "end": v(4.9, 9.23) * mm});
            skLineSegment(sketch, "E117.1.7", {"start": v(12.73, 6.36) * mm, "end": v(9.23, 4.9) * mm});
            skLineSegment(sketch, "E117.2.0", {"start": v(-10.72, 28.5) * mm, "end": v(10.72, 28.5) * mm});
            skLineSegment(sketch, "E117.2.1", {"start": v(-6.17, 17.5) * mm, "end": v(-10.72, 28.5) * mm});
            skLineSegment(sketch, "E117.2.2", {"start": v(6.17, 17.5) * mm, "end": v(-6.17, 17.5) * mm});
            skLineSegment(sketch, "E117.2.3", {"start": v(10.72, 28.5) * mm, "end": v(6.17, 17.5) * mm});
            skLineSegment(sketch, "E117.2.4", {"start": v(-4.5, 13.5) * mm, "end": v(4.5, 13.5) * mm});
            skLineSegment(sketch, "E117.2.5", {"start": v(-3.06, 10) * mm, "end": v(-4.5, 13.5) * mm});
            skLineSegment(sketch, "E117.2.6", {"start": v(3.06, 10) * mm, "end": v(-3.06, 10) * mm});
            skLineSegment(sketch, "E117.2.7", {"start": v(4.5, 13.5) * mm, "end": v(3.06, 10) * mm});
            skLineSegment(sketch, "E117.3.0", {"start": v(-27.73, 12.57) * mm, "end": v(-12.57, 27.73) * mm});
            skLineSegment(sketch, "E117.3.1", {"start": v(-16.73, 8.01) * mm, "end": v(-27.73, 12.57) * mm});
            skLineSegment(sketch, "E117.3.2", {"start": v(-8.01, 16.73) * mm, "end": v(-16.73, 8.01) * mm});
            skLineSegment(sketch, "E117.3.3", {"start": v(-12.57, 27.73) * mm, "end": v(-8.01, 16.73) * mm});
            skLineSegment(sketch, "E117.3.4", {"start": v(-12.73, 6.36) * mm, "end": v(-6.36, 12.73) * mm});
            skLineSegment(sketch, "E117.3.5", {"start": v(-9.23, 4.9) * mm, "end": v(-12.73, 6.36) * mm});
            skLineSegment(sketch, "E117.3.6", {"start": v(-4.9, 9.23) * mm, "end": v(-9.23, 4.9) * mm});
            skLineSegment(sketch, "E117.3.7", {"start": v(-6.36, 12.73) * mm, "end": v(-4.9, 9.23) * mm});
            skLineSegment(sketch, "E117.4.0", {"start": v(-28.5, -10.72) * mm, "end": v(-28.5, 10.72) * mm});
            skLineSegment(sketch, "E117.4.1", {"start": v(-17.5, -6.17) * mm, "end": v(-28.5, -10.72) * mm});
            skLineSegment(sketch, "E117.4.2", {"start": v(-17.5, 6.17) * mm, "end": v(-17.5, -6.17) * mm});
            skLineSegment(sketch, "E117.4.3", {"start": v(-28.5, 10.72) * mm, "end": v(-17.5, 6.17) * mm});
            skLineSegment(sketch, "E117.4.4", {"start": v(-13.5, -4.5) * mm, "end": v(-13.5, 4.5) * mm});
            skLineSegment(sketch, "E117.4.5", {"start": v(-10, -3.06) * mm, "end": v(-13.5, -4.5) * mm});
            skLineSegment(sketch, "E117.4.6", {"start": v(-10, 3.06) * mm, "end": v(-10, -3.06) * mm});
            skLineSegment(sketch, "E117.4.7", {"start": v(-13.5, 4.5) * mm, "end": v(-10, 3.06) * mm});
            skLineSegment(sketch, "E117.5.0", {"start": v(-12.57, -27.73) * mm, "end": v(-27.73, -12.57) * mm});
            skLineSegment(sketch, "E117.5.1", {"start": v(-8.01, -16.73) * mm, "end": v(-12.57, -27.73) * mm});
            skLineSegment(sketch, "E117.5.2", {"start": v(-16.73, -8.01) * mm, "end": v(-8.01, -16.73) * mm});
            skLineSegment(sketch, "E117.5.3", {"start": v(-27.73, -12.57) * mm, "end": v(-16.73, -8.01) * mm});
            skLineSegment(sketch, "E117.5.4", {"start": v(-6.36, -12.73) * mm, "end": v(-12.73, -6.36) * mm});
            skLineSegment(sketch, "E117.5.5", {"start": v(-4.9, -9.23) * mm, "end": v(-6.36, -12.73) * mm});
            skLineSegment(sketch, "E117.5.6", {"start": v(-9.23, -4.9) * mm, "end": v(-4.9, -9.23) * mm});
            skLineSegment(sketch, "E117.5.7", {"start": v(-12.73, -6.36) * mm, "end": v(-9.23, -4.9) * mm});
            skLineSegment(sketch, "E117.6.0", {"start": v(10.72, -28.5) * mm, "end": v(-10.72, -28.5) * mm});
            skLineSegment(sketch, "E117.6.1", {"start": v(6.17, -17.5) * mm, "end": v(10.72, -28.5) * mm});
            skLineSegment(sketch, "E117.6.2", {"start": v(-6.17, -17.5) * mm, "end": v(6.17, -17.5) * mm});
            skLineSegment(sketch, "E117.6.3", {"start": v(-10.72, -28.5) * mm, "end": v(-6.17, -17.5) * mm});
            skLineSegment(sketch, "E117.6.4", {"start": v(4.5, -13.5) * mm, "end": v(-4.5, -13.5) * mm});
            skLineSegment(sketch, "E117.6.5", {"start": v(3.06, -10) * mm, "end": v(4.5, -13.5) * mm});
            skLineSegment(sketch, "E117.6.6", {"start": v(-3.06, -10) * mm, "end": v(3.06, -10) * mm});
            skLineSegment(sketch, "E117.6.7", {"start": v(-4.5, -13.5) * mm, "end": v(-3.06, -10) * mm});
            skLineSegment(sketch, "E117.7.0", {"start": v(27.73, -12.57) * mm, "end": v(12.57, -27.73) * mm});
            skLineSegment(sketch, "E117.7.1", {"start": v(16.73, -8.01) * mm, "end": v(27.73, -12.57) * mm});
            skLineSegment(sketch, "E117.7.2", {"start": v(8.01, -16.73) * mm, "end": v(16.73, -8.01) * mm});
            skLineSegment(sketch, "E117.7.3", {"start": v(12.57, -27.73) * mm, "end": v(8.01, -16.73) * mm});
            skLineSegment(sketch, "E117.7.4", {"start": v(12.73, -6.36) * mm, "end": v(6.36, -12.73) * mm});
            skLineSegment(sketch, "E117.7.5", {"start": v(9.23, -4.9) * mm, "end": v(12.73, -6.36) * mm});
            skLineSegment(sketch, "E117.7.6", {"start": v(4.9, -9.23) * mm, "end": v(9.23, -4.9) * mm});
            skLineSegment(sketch, "E117.7.7", {"start": v(6.36, -12.73) * mm, "end": v(4.9, -9.23) * mm});
            skPoint(sketch, "E117.center", {"position": v(0, 0) * mm});
            skSolve(sketch);
        }
        {
            var Q0;
            Q0=qSketchRegion(id+"F29",true);
            extrude(context, id + "F30", {"entities" : qUnion([Q0]), "operationType" : NewBodyOperationType.REMOVE, "oppositeDirection" : true, "depth" : 25 * mm});
        }
    });
